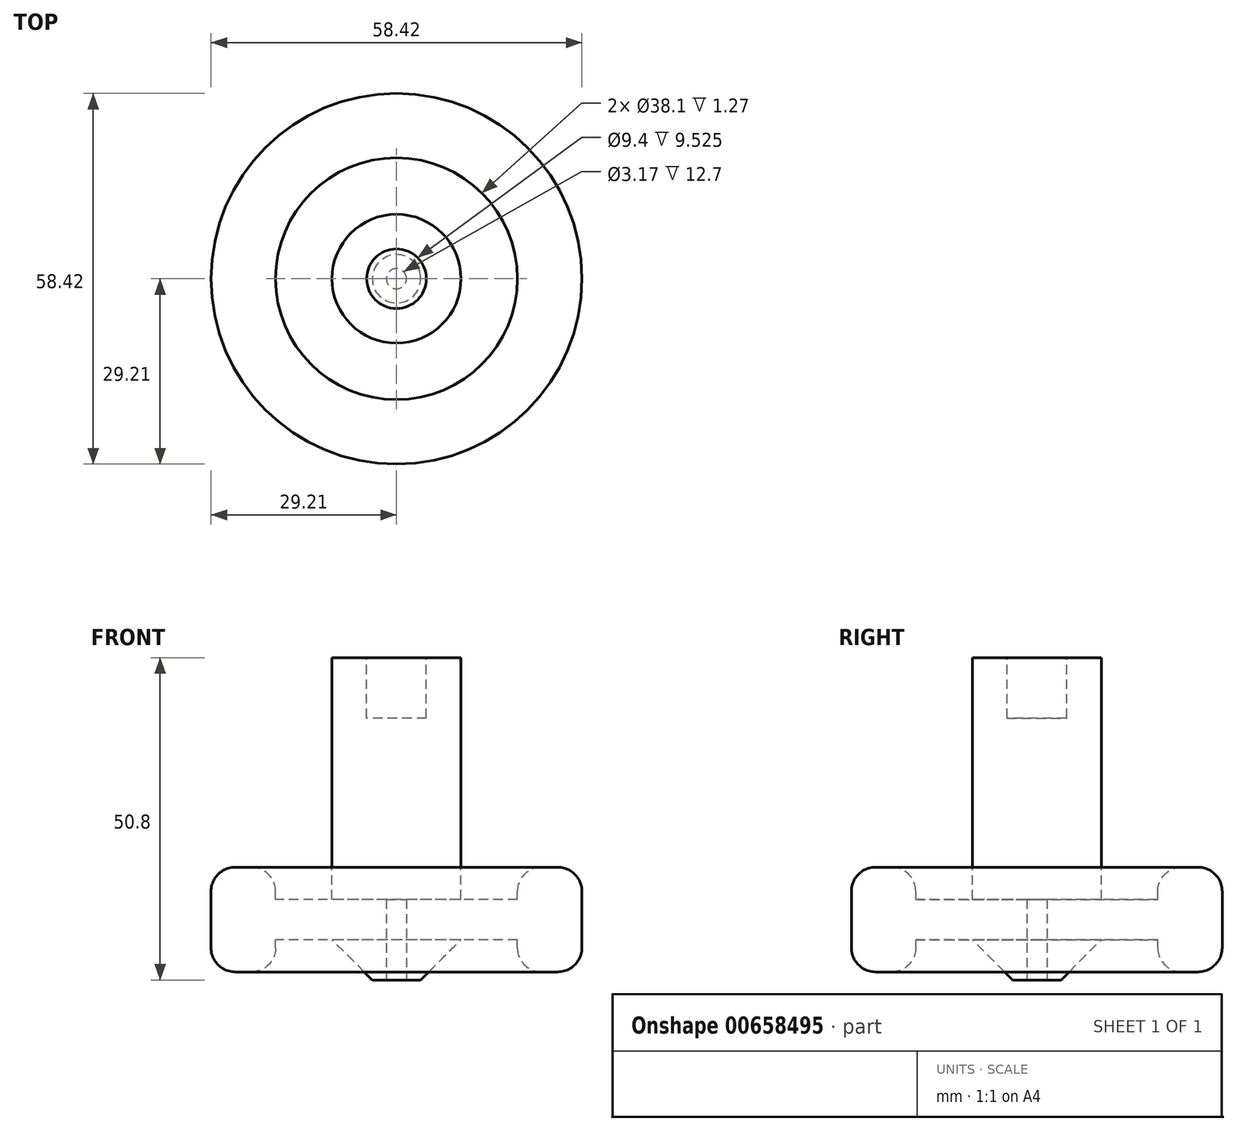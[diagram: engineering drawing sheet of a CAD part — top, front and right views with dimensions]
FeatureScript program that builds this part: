
annotation { "Feature Type Name" : "Feature", "Feature Type Description" : "" }
export const myFeature = defineFeature(function(context is Context, id is Id, definition is map)
    precondition{}
    {
        {
            var Q0;
            Q0=qCreatedBy(makeId("Front.planeOp"),FACE);
            var sketch = newSketch(context, id + "F0", { "sketchPlane" : qUnion([Q0])});
            skLineSegment(sketch, "E0", {"start": v(0, 0) * mm, "end": v(3.81, 0) * mm});
            skLineSegment(sketch, "E1", {"start": v(10.16, 12.7) * mm, "end": v(19.05, 12.7) * mm});
            skLineSegment(sketch, "E2", {"start": v(19.05, 6.35) * mm, "end": v(10.16, 6.35) * mm});
            skLineSegment(sketch, "E3", {"start": v(10.16, 12.7) * mm, "end": v(10.16, 50.8) * mm});
            skLineSegment(sketch, "E4", {"start": v(10.16, 50.8) * mm, "end": v(0, 50.8) * mm});
            skLineSegment(sketch, "E5", {"start": v(0, 50.8) * mm, "end": v(0, 0) * mm});
            skLineSegment(sketch, "E6", {"start": v(19.05, 12.7) * mm, "end": v(19.05, 13.97) * mm});
            skLineSegment(sketch, "E7", {"start": v(22.86, 17.78) * mm, "end": v(25.4, 17.78) * mm});
            skLineSegment(sketch, "E8", {"start": v(29.21, 13.97) * mm, "end": v(29.21, 5.08) * mm});
            skLineSegment(sketch, "E9", {"start": v(25.4, 1.27) * mm, "end": v(22.86, 1.27) * mm});
            skLineSegment(sketch, "E10", {"start": v(19.05, 5.08) * mm, "end": v(19.05, 6.35) * mm});
            skPoint(sketch, "E11.visualSharp", {"position": v(19.05, 17.78) * mm});
            skArc(sketch, "E11.filletArc", {"start": v(22.86, 17.78) * mm, "mid": v(20.17, 16.66) * mm, "end": v(19.05, 13.97) * mm});
            skPoint(sketch, "E12.visualSharp", {"position": v(29.21, 17.78) * mm});
            skArc(sketch, "E12.filletArc", {"start": v(29.21, 13.97) * mm, "mid": v(28.1, 16.66) * mm, "end": v(25.4, 17.78) * mm});
            skPoint(sketch, "E13.visualSharp", {"position": v(29.21, 1.27) * mm});
            skArc(sketch, "E13.filletArc", {"start": v(25.4, 1.27) * mm, "mid": v(28.1, 2.39) * mm, "end": v(29.21, 5.08) * mm});
            skPoint(sketch, "E14.visualSharp", {"position": v(19.05, 1.27) * mm});
            skArc(sketch, "E14.filletArc", {"start": v(19.05, 5.08) * mm, "mid": v(20.17, 2.39) * mm, "end": v(22.86, 1.27) * mm});
            skLineSegment(sketch, "E15", {"start": v(10.16, 6.35) * mm, "end": v(3.81, 0) * mm});
            skPoint(sketch, "E16.orphan", {"position": v(10.16, 0) * mm});
            skSolve(sketch);
        }
        {
            var Q0;
            Q0=qSketchRegion(id+"F0",true);
            var Q1;
            Q1=sQuery(id+"F0.wireOp",EDGE,"E5");
            revolve(context, id + "F1", {"entities" : qUnion([Q0]), "axis" : qUnion([Q1]), "revolveType" : RevolveType.FULL});
        }
        {
            var Q0;
            Q0=makeQuery(id+"F1.opRevolve","SWEPT_FACE",FACE,{"disambiguationData":[OSD([sQuery(id+"F0.wireOp",EDGE,"E4")])]});
            var sketch = newSketch(context, id + "F2", { "sketchPlane" : qUnion([Q0])});
            skCircle(sketch, "E17", {"center": v(0, 0) * mm, "radius": 4.7 * mm});
            skSolve(sketch);
        }
        {
            var Q0;
            Q0=qSketchRegion(id+"F2",true);
            extrude(context, id + "F3", {"entities" : qUnion([Q0]), "operationType" : NewBodyOperationType.REMOVE, "oppositeDirection" : true, "depth" : 9.52 * mm, "offsetDistance" : 25.4 * mm});
        }
        {
            var Q0;
            Q0=makeQuery(id+"F1.opRevolve","SWEPT_FACE",FACE,{"disambiguationData":[OSD([sQuery(id+"F0.wireOp",EDGE,"E0")])]});
            var sketch = newSketch(context, id + "F4", { "sketchPlane" : qUnion([Q0])});
            skCircle(sketch, "E18", {"center": v(0, 0) * mm, "radius": 1.59 * mm});
            skSolve(sketch);
        }
        {
            var Q0;
            Q0=qSketchRegion(id+"F4",true);
            extrude(context, id + "F5", {"entities" : qUnion([Q0]), "operationType" : NewBodyOperationType.REMOVE, "oppositeDirection" : true, "depth" : 12.7 * mm, "offsetDistance" : 25.4 * mm});
        }
    });
